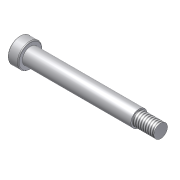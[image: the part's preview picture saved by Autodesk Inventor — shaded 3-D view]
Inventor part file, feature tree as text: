
AUTODESK INVENTOR PART (.ipt)
format: ipt  version: 2012 (Build 160160000, 160)  size: 109,568 bytes
history: native  units: in
note: dims shown in document units (in); Inventor stores cm internally (conversion verified against a paired STEP export)
features: sketch x2, revolve x1, fillet x1, thread x1, extrude x1
ambient origin geometry x8: Origin, YZ Plane, XZ Plane, XY Plane, X Axis, Y Axis, Z Axis, Center Point
bodies: Solid1 (feature_tree)
feature tree (6):
  revolve  "Revolution1"  [1 undecoded]
  fillet  "Fillet1"  Radius=0.1562in
  thread  "Thread1"  [1 undecoded]
  extrude  "Extrusion1"  Depth=0.5in
  sketch  "Sketch1"  dims[d0=0.2812in d1=0.1875in d2=0.1562in d3=0.25in]
  sketch  "Sketch2"  dims[d4=2.5in d5=0.5in d6=90.0deg d7=0.02in d8=1.0in d9=0.0in d10=0.1875in d11=0.125in d12=0.0in]
note: 2 required parameter values undecoded (feature->parameter linkage not recoverable at this tier; creation-order binding heuristic only, values carry confidence <= 0.55)